# Revit family: Cleanout_Housing-Zurn-Z1474-Heavy-Duty
name_source: partatom
category: Plumbing Fixtures
units: mm (PartAtom-declared; Revit-internal decimal feet)

## family parameters
Always vertical = Yes
Cut with Voids When Loaded = No
Maintain Annotation Orientation = No
OmniClass Number = 23.45.55.21
OmniClass Title = Drains (Wastes)
Part Type = Normal
Room Calculation Point = No
Round Connector Dimension = Use Radius
Shared = No
Work Plane-Based = No

## types (2) — shared parameters
A_ Pipe Size (Actual-Inner) = 8.375 "
A_ Pipe Size (Actual-Outer) = 8.875 "
Approx. Weight (Lbs) = 38 "
Assembly Code = D2030300
CW Connection = No
Connector Radius = 4.188 "
Default Elevation = 4 "
Description = HEAVY DUTY CLEANOUT HOUSING
Frame Height = 2.75 "
HW Connection = No
Main Material = Iron - Zurn - Cast - Painted - Blue
Manufacturer = Zurn Water, LLC
Manufacurer Brand = Zurn
Modified Date = 12/16/2025
Product Documentation Link = https://files.zurn.com
Product Page URL = https://www.zurn.com
Product data url = https://www.bimobject.com
Trap Primer = Yes
URL = www.zurn.com
Vent Connection = No
Waste Connection = Yes
zero-valued in all types: CWFU, HWFU, WFU

## per-type parameters (varying)
| type | E_ Body Height | Grate Material | Top diameter | ZN-Top |
| Z1474 | 11 " | Iron - Zurn - Cast - Painted - Blue | 9 " | No |
| ZN1474 | 11.188 " | Bronze - Zurn - Polished Nickel | 9.75 " | Yes |

note: column(s) folded — value = type name in every type: Model

## geometry (parser evidence)
native form markers: Blend x8, Sweep x4
no freeform markers — native parametric forms only
